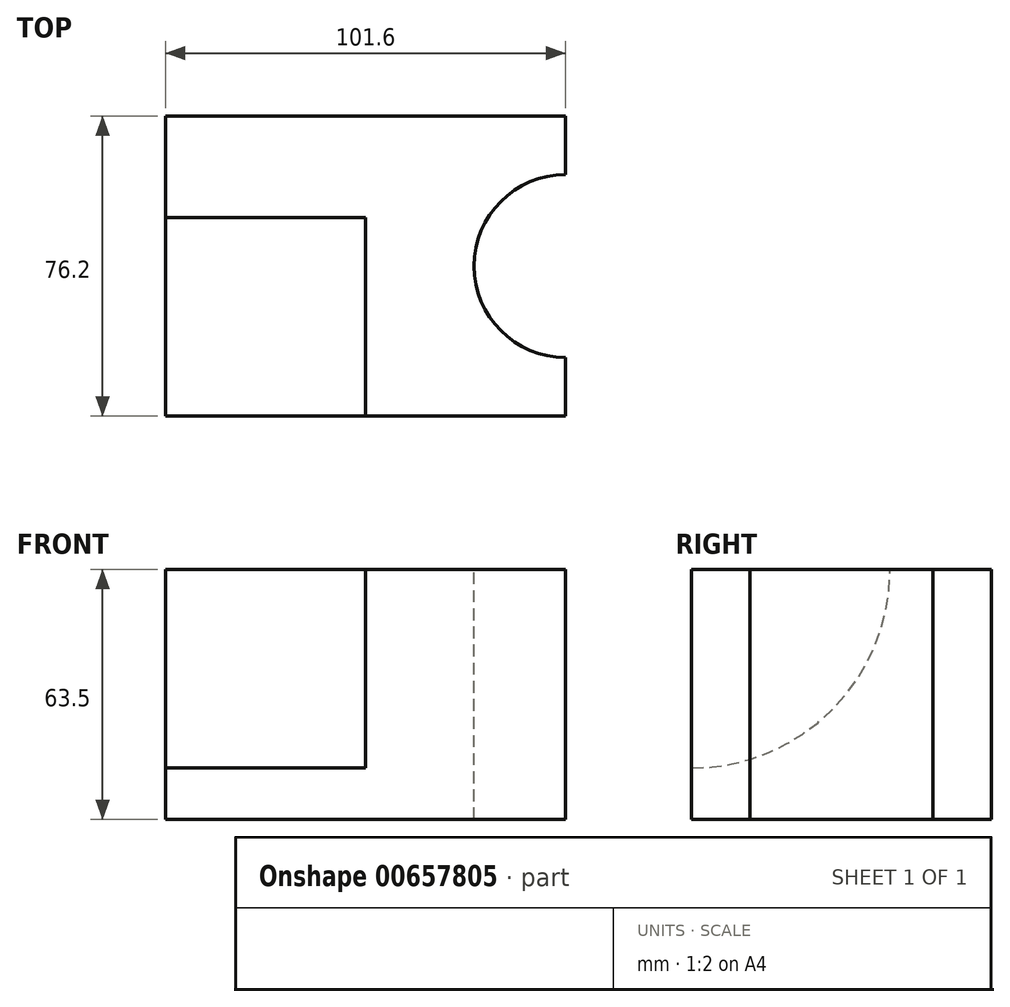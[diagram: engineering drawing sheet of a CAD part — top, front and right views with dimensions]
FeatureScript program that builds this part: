
annotation { "Feature Type Name" : "Feature", "Feature Type Description" : "" }
export const myFeature = defineFeature(function(context is Context, id is Id, definition is map)
    precondition{}
    {
        {
            var Q0;
            Q0=qCreatedBy(makeId("Top.planeOp"),FACE);
            var sketch = newSketch(context, id + "F0", { "sketchPlane" : qUnion([Q0])});
            skLineSegment(sketch, "E0.bottom", {"start": v(32.98, -13.95) * mm, "end": v(134.58, -13.95) * mm});
            skLineSegment(sketch, "E0.top", {"start": v(32.98, -90.15) * mm, "end": v(134.58, -90.15) * mm});
            skLineSegment(sketch, "E0.left", {"start": v(32.98, -13.95) * mm, "end": v(32.98, -90.15) * mm});
            skLineSegment(sketch, "E0.right", {"start": v(134.58, -13.95) * mm, "end": v(134.58, -90.15) * mm});
            skSolve(sketch);
        }
        {
            var Q0;
            Q0 = qSketchRegion(id + "F0", true);
            extrude(context, id + "F1", {"entities" : qUnion([Q0]), "depth" : 63.5 * mm, "offsetDistance" : 25.4 * mm});
        }
        {
            var Q0;
            Q0=makeQuery(id+"F1.opExtrude","CAP_FACE",FACE,{"disambiguationData":[OSD([sQuery(id+"F0.wireOp",EDGE,"E0.bottom"),sQuery(id+"F0.wireOp",EDGE,"E0.top"),sQuery(id+"F0.wireOp",EDGE,"E0.left"),sQuery(id+"F0.wireOp",EDGE,"E0.right")])],"isStart":false});
            var sketch = newSketch(context, id + "F2", { "sketchPlane" : qUnion([Q0])});
            skCircle(sketch, "E1", {"center": v(134.58, -52.05) * mm, "radius": 23.24 * mm});
            skSolve(sketch);
        }
        {
            var Q0;
            {var subQ0=sQuery(id+"F2.wireOp",EDGE,"E1");var subQ1=makeQuery(id+"F1.opExtrude","CAP_EDGE",EDGE,{"disambiguationData":[OSD([sQuery(id+"F0.wireOp",EDGE,"E0.right")])],"isStart":false});var subQ2=makeQuery(id+"F2.imprint","INTERSECT",VERTEX,{"disambiguationData":[OD(0.0)],"derivedFrom":[subQ1,subQ0]});Q0=makeQuery(id+"F2.imprint","IMPRINT",FACE,{"disambiguationData":[TD([[makeQuery(id+"F2.imprint","IMPRINT",EDGE,{"disambiguationData":[TD([[subQ2,1.0]])],"derivedFrom":subQ0}),1.0]])]});}
            var Q1;
            {var subQ0=sQuery(id+"F2.wireOp",EDGE,"E1");var subQ1=makeQuery(id+"F1.opExtrude","CAP_EDGE",EDGE,{"disambiguationData":[OSD([sQuery(id+"F0.wireOp",EDGE,"E0.right")])],"isStart":false});var subQ2=makeQuery(id+"F2.imprint","INTERSECT",VERTEX,{"disambiguationData":[OD(0.0)],"derivedFrom":[subQ1,subQ0]});Q1=makeQuery(id+"F2.imprint","IMPRINT",FACE,{"disambiguationData":[TD([[makeQuery(id+"F2.imprint","IMPRINT",EDGE,{"disambiguationData":[TD([[subQ2,-1.0]])],"derivedFrom":subQ0}),1.0]])]});}
            extrude(context, id + "F3", {"entities" : qUnion([Q0, Q1]), "operationType" : NewBodyOperationType.REMOVE, "oppositeDirection" : true, "depth" : 71.63 * mm, "offsetDistance" : 25.4 * mm});
        }
        {
            var Q0;
            Q0=makeQuery(id+"F1.opExtrude","SWEPT_FACE",FACE,{"disambiguationData":[OSD([sQuery(id+"F0.wireOp",EDGE,"E0.left")])]});
            var sketch = newSketch(context, id + "F4", { "sketchPlane" : qUnion([Q0])});
            skCircle(sketch, "E2", {"center": v(90.15, 63.5) * mm, "radius": 50.47 * mm});
            skSolve(sketch);
        }
        {
            var Q0;
            Q0 = qSketchRegion(id + "F4", true);
            extrude(context, id + "F5", {"entities" : qUnion([Q0]), "operationType" : NewBodyOperationType.REMOVE, "oppositeDirection" : true, "depth" : 50.8 * mm, "offsetDistance" : 25.4 * mm});
        }
    });
